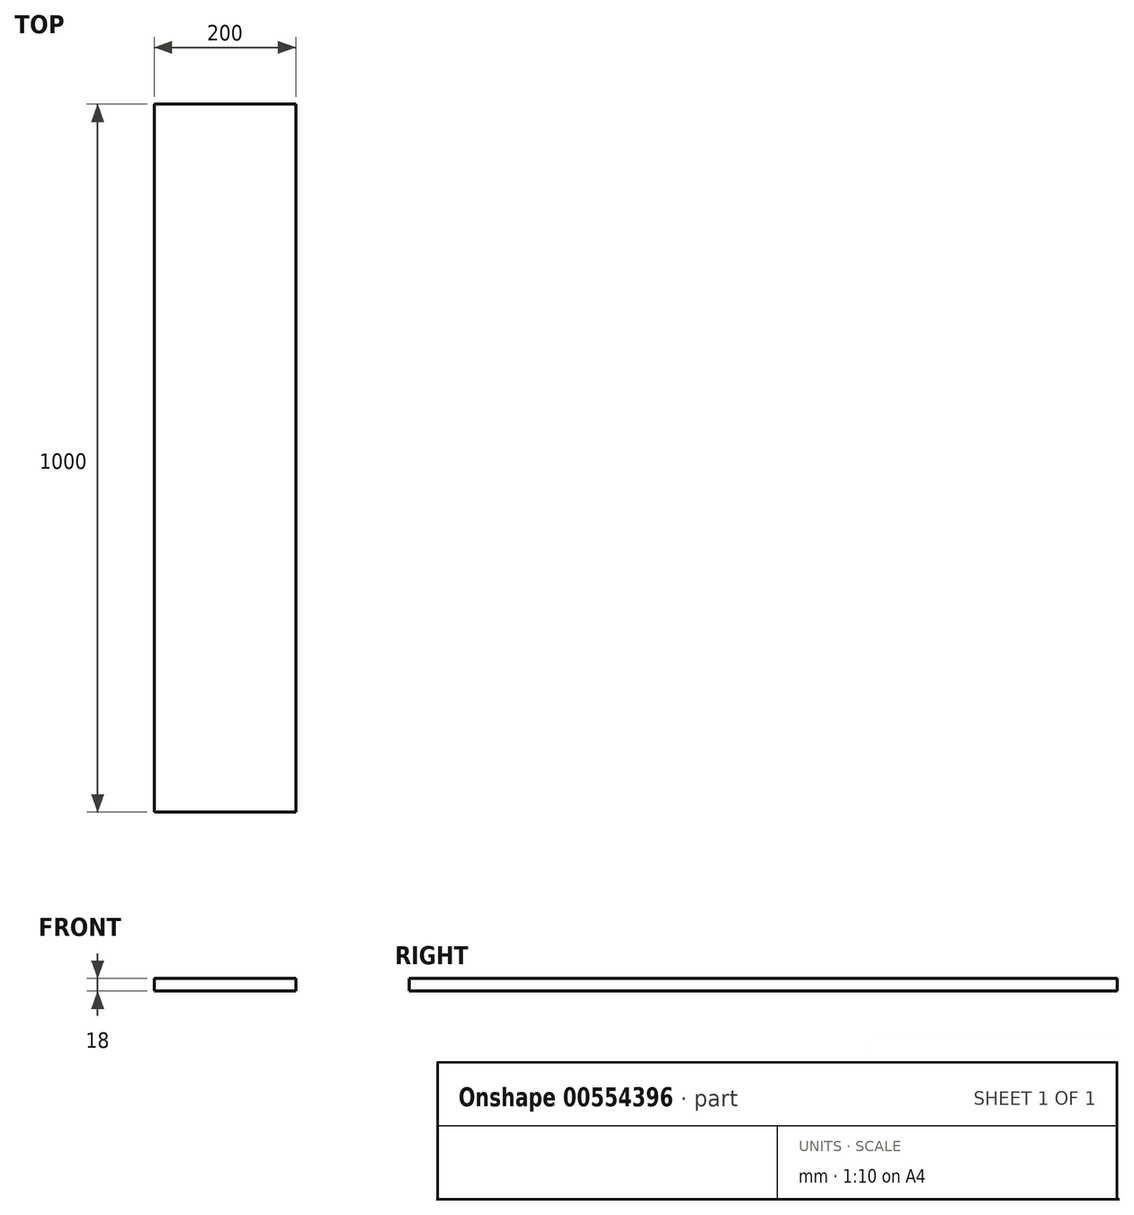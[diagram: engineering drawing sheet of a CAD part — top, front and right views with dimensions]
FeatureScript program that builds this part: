
annotation { "Feature Type Name" : "Feature", "Feature Type Description" : "" }
export const myFeature = defineFeature(function(context is Context, id is Id, definition is map)
    precondition{}
    {
        {
            var Q0;
            Q0=qCreatedBy(makeId("Top.planeOp"),FACE);
            var sketch = newSketch(context, id + "F0", { "sketchPlane" : qUnion([Q0])});
            skLineSegment(sketch, "E0.bottom", {"start": v(0, 0) * mm, "end": v(200, 0) * mm});
            skLineSegment(sketch, "E0.top", {"start": v(0, 1000) * mm, "end": v(200, 1000) * mm});
            skLineSegment(sketch, "E0.left", {"start": v(0, 0) * mm, "end": v(0, 1000) * mm});
            skLineSegment(sketch, "E0.right", {"start": v(200, 0) * mm, "end": v(200, 1000) * mm});
            skSolve(sketch);
        }
        {
            var Q0;
            Q0=makeQuery(id+"F0.imprint","IMPRINT",FACE,{"disambiguationData":[TD([[makeQuery(id+"F0.imprint","IMPRINT",EDGE,{"derivedFrom":sQuery(id+"F0.wireOp",EDGE,"E0.bottom")}),1.0]])]});
            extrude(context, id + "F1", {"entities" : qUnion([Q0]), "depth" : 18 * mm, "offsetDistance" : 25 * mm});
        }
    });
